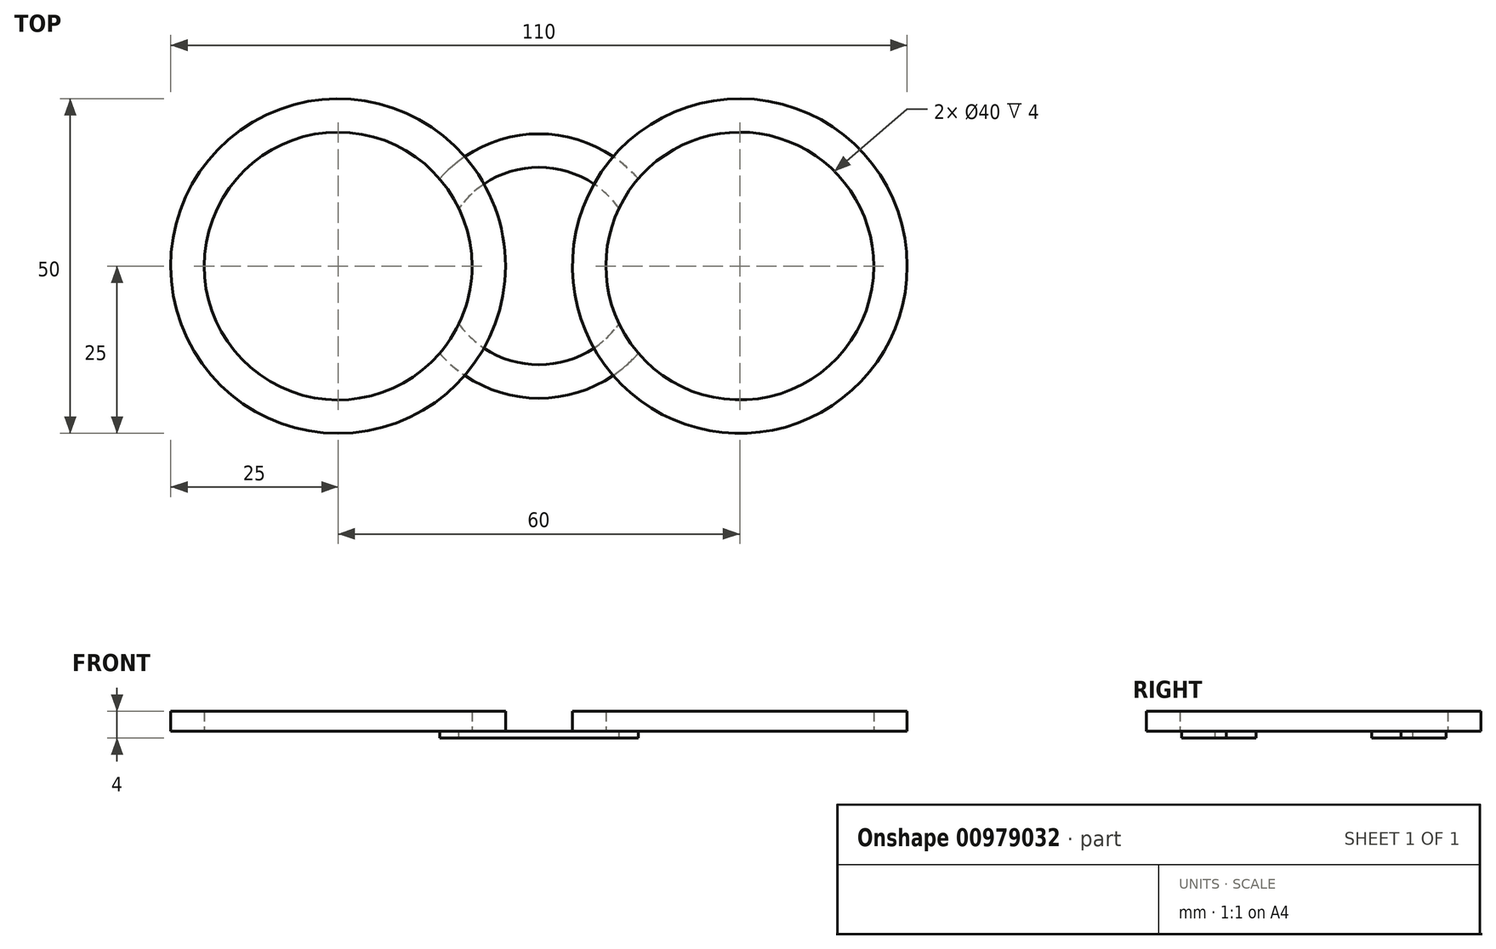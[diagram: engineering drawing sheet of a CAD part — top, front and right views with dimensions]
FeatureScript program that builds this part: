
annotation { "Feature Type Name" : "Feature", "Feature Type Description" : "" }
export const myFeature = defineFeature(function(context is Context, id is Id, definition is map)
    precondition{}
    {
        {
            var Q0;
            Q0=qCreatedBy(makeId("Top.planeOp"),FACE);
            var sketch = newSketch(context, id + "F0", { "sketchPlane" : qUnion([Q0])});
            skCircle(sketch, "E0", {"center": v(0, 0) * mm, "radius": 19.75 * mm});
            skCircle(sketch, "E1", {"center": v(0, 0) * mm, "radius": 14.75 * mm});
            skSolve(sketch);
        }
        {
            var Q0;
            Q0=makeQuery(id+"F0.imprint","IMPRINT",FACE,{"disambiguationData":[TD([[makeQuery(id+"F0.imprint","IMPRINT",EDGE,{"derivedFrom":sQuery(id+"F0.wireOp",EDGE,"E0")}),1.0]])]});
            extrude(context, id + "F1", {"entities" : qUnion([Q0]), "depth" : 1 * mm, "offsetDistance" : 25 * mm});
        }
        {
            var Q0;
            Q0=makeQuery(id+"F1.opExtrude","CAP_FACE",FACE,{"disambiguationData":[OSD([sQuery(id+"F0.wireOp",EDGE,"E0"),sQuery(id+"F0.wireOp",EDGE,"E1")])],"isStart":false});
            var sketch = newSketch(context, id + "F2", { "sketchPlane" : qUnion([Q0])});
            skCircle(sketch, "E2", {"center": v(-30, 0) * mm, "radius": 20 * mm});
            skCircle(sketch, "E3", {"center": v(30, 0) * mm, "radius": 20 * mm});
            skCircle(sketch, "E4", {"center": v(-30, 0) * mm, "radius": 25 * mm});
            skCircle(sketch, "E5", {"center": v(30, 0) * mm, "radius": 25 * mm});
            skSolve(sketch);
        }
        {
            var Q0;
            {var subQ0=sQuery(id+"F2.wireOp",EDGE,"E2");var subQ1=makeQuery(id+"F1.opExtrude","CAP_EDGE",EDGE,{"disambiguationData":[OSD([sQuery(id+"F0.wireOp",EDGE,"E0")])],"isStart":false});var subQ2=makeQuery(id+"F2.imprint","INTERSECT",VERTEX,{"disambiguationData":[OD(0.0)],"derivedFrom":[subQ1,subQ0]});Q0=makeQuery(id+"F2.imprint","IMPRINT",FACE,{"disambiguationData":[TD([[makeQuery(id+"F2.imprint","IMPRINT",EDGE,{"disambiguationData":[TD([[subQ2,-1.0]])],"derivedFrom":subQ0}),-1.0]])]});}
            var Q1;
            {var subQ0=sQuery(id+"F2.wireOp",EDGE,"E2");var subQ1=makeQuery(id+"F1.opExtrude","CAP_EDGE",EDGE,{"disambiguationData":[OSD([sQuery(id+"F0.wireOp",EDGE,"E1")])],"isStart":false});var subQ2=makeQuery(id+"F2.imprint","INTERSECT",VERTEX,{"disambiguationData":[OD(0.0)],"derivedFrom":[subQ1,subQ0]});Q1=makeQuery(id+"F2.imprint","IMPRINT",FACE,{"disambiguationData":[TD([[makeQuery(id+"F2.imprint","IMPRINT",EDGE,{"disambiguationData":[TD([[subQ2,1.0]])],"derivedFrom":subQ0}),-1.0]])]});}
            var Q2;
            {var subQ0=sQuery(id+"F2.wireOp",EDGE,"E2");var subQ1=makeQuery(id+"F1.opExtrude","CAP_EDGE",EDGE,{"disambiguationData":[OSD([sQuery(id+"F0.wireOp",EDGE,"E0")])],"isStart":false});var subQ2=makeQuery(id+"F2.imprint","INTERSECT",VERTEX,{"disambiguationData":[OD(0.0)],"derivedFrom":[subQ1,subQ0]});Q2=makeQuery(id+"F2.imprint","IMPRINT",FACE,{"disambiguationData":[TD([[makeQuery(id+"F2.imprint","IMPRINT",EDGE,{"disambiguationData":[TD([[subQ2,1.0]])],"derivedFrom":subQ0}),-1.0]])]});}
            var Q3;
            {var subQ0=sQuery(id+"F2.wireOp",EDGE,"E2");var subQ1=makeQuery(id+"F1.opExtrude","CAP_EDGE",EDGE,{"disambiguationData":[OSD([sQuery(id+"F0.wireOp",EDGE,"E0")])],"isStart":false});var subQ2=makeQuery(id+"F2.imprint","INTERSECT",VERTEX,{"disambiguationData":[OD(1.0)],"derivedFrom":[subQ1,subQ0]});Q3=makeQuery(id+"F2.imprint","IMPRINT",FACE,{"disambiguationData":[TD([[makeQuery(id+"F2.imprint","IMPRINT",EDGE,{"disambiguationData":[TD([[subQ2,-1.0]])],"derivedFrom":subQ0}),-1.0]])]});}
            var Q4;
            {var subQ0=sQuery(id+"F2.wireOp",EDGE,"E3");var subQ1=makeQuery(id+"F1.opExtrude","CAP_EDGE",EDGE,{"disambiguationData":[OSD([sQuery(id+"F0.wireOp",EDGE,"E0")])],"isStart":false});var subQ2=makeQuery(id+"F2.imprint","INTERSECT",VERTEX,{"disambiguationData":[OD(0.0)],"derivedFrom":[subQ1,subQ0]});Q4=makeQuery(id+"F2.imprint","IMPRINT",FACE,{"disambiguationData":[TD([[makeQuery(id+"F2.imprint","IMPRINT",EDGE,{"disambiguationData":[TD([[subQ2,1.0]])],"derivedFrom":subQ0}),-1.0]])]});}
            var Q5;
            {var subQ0=sQuery(id+"F2.wireOp",EDGE,"E3");var subQ1=makeQuery(id+"F1.opExtrude","CAP_EDGE",EDGE,{"disambiguationData":[OSD([sQuery(id+"F0.wireOp",EDGE,"E1")])],"isStart":false});var subQ2=makeQuery(id+"F2.imprint","INTERSECT",VERTEX,{"disambiguationData":[OD(1.0)],"derivedFrom":[subQ1,subQ0]});Q5=makeQuery(id+"F2.imprint","IMPRINT",FACE,{"disambiguationData":[TD([[makeQuery(id+"F2.imprint","IMPRINT",EDGE,{"disambiguationData":[TD([[subQ2,-1.0]])],"derivedFrom":subQ0}),-1.0]])]});}
            var Q6;
            {var subQ0=sQuery(id+"F2.wireOp",EDGE,"E3");var subQ1=makeQuery(id+"F1.opExtrude","CAP_EDGE",EDGE,{"disambiguationData":[OSD([sQuery(id+"F0.wireOp",EDGE,"E1")])],"isStart":false});var subQ2=makeQuery(id+"F2.imprint","INTERSECT",VERTEX,{"disambiguationData":[OD(0.0)],"derivedFrom":[subQ1,subQ0]});Q6=makeQuery(id+"F2.imprint","IMPRINT",FACE,{"disambiguationData":[TD([[makeQuery(id+"F2.imprint","IMPRINT",EDGE,{"disambiguationData":[TD([[subQ2,-1.0]])],"derivedFrom":subQ0}),-1.0]])]});}
            var Q7;
            {var subQ0=sQuery(id+"F2.wireOp",EDGE,"E3");var subQ1=makeQuery(id+"F1.opExtrude","CAP_EDGE",EDGE,{"disambiguationData":[OSD([sQuery(id+"F0.wireOp",EDGE,"E1")])],"isStart":false});var subQ2=makeQuery(id+"F2.imprint","INTERSECT",VERTEX,{"disambiguationData":[OD(0.0)],"derivedFrom":[subQ1,subQ0]});Q7=makeQuery(id+"F2.imprint","IMPRINT",FACE,{"disambiguationData":[TD([[makeQuery(id+"F2.imprint","IMPRINT",EDGE,{"disambiguationData":[TD([[subQ2,1.0]])],"derivedFrom":subQ0}),-1.0]])]});}
            extrude(context, id + "F3", {"entities" : qUnion([Q0, Q1, Q2, Q3, Q4, Q5, Q6, Q7]), "operationType" : NewBodyOperationType.ADD, "depth" : 3 * mm, "offsetDistance" : 25 * mm});
        }
        {
            var Q0;
            {var subQ0=sQuery(id+"F0.wireOp",EDGE,"E0");var subQ1=sQuery(id+"F0.wireOp",EDGE,"E1");var subQ2=sQuery(id+"F2.wireOp",EDGE,"E3");Q0=makeQuery(id+"F3.boolean.opBoolean","SPLIT",FACE,{"disambiguationData":[TD([makeQuery(id+"F1.opExtrude","SWEPT_FACE",FACE,{"disambiguationData":[OSD([subQ0])]}),makeQuery(id+"F1.opExtrude","SWEPT_FACE",FACE,{"disambiguationData":[OSD([subQ1])]}),makeQuery(id+"F3.opExtrude","SWEPT_FACE",FACE,{"disambiguationData":[OSD([subQ2])]}),makeQuery(id+"F3.opExtrude","CAP_FACE",FACE,{"disambiguationData":[OSD([subQ2,sQuery(id+"F2.wireOp",EDGE,"E5")])],"isStart":true})])],"derivedFrom":makeQuery(id+"F1.opExtrude","CAP_FACE",FACE,{"disambiguationData":[OSD([subQ0,subQ1])],"isStart":false})});}
            var Q1;
            {var subQ0=sQuery(id+"F0.wireOp",EDGE,"E0");var subQ1=sQuery(id+"F0.wireOp",EDGE,"E1");var subQ2=sQuery(id+"F2.wireOp",EDGE,"E2");Q1=makeQuery(id+"F3.boolean.opBoolean","SPLIT",FACE,{"disambiguationData":[TD([makeQuery(id+"F1.opExtrude","SWEPT_FACE",FACE,{"disambiguationData":[OSD([subQ0])]}),makeQuery(id+"F1.opExtrude","SWEPT_FACE",FACE,{"disambiguationData":[OSD([subQ1])]}),makeQuery(id+"F3.opExtrude","SWEPT_FACE",FACE,{"disambiguationData":[OSD([subQ2])]}),makeQuery(id+"F3.opExtrude","CAP_FACE",FACE,{"disambiguationData":[OSD([subQ2,sQuery(id+"F2.wireOp",EDGE,"E4")])],"isStart":true})])],"derivedFrom":makeQuery(id+"F1.opExtrude","CAP_FACE",FACE,{"disambiguationData":[OSD([subQ0,subQ1])],"isStart":false})});}
            extrude(context, id + "F4", {"entities" : qUnion([Q0, Q1]), "operationType" : NewBodyOperationType.REMOVE, "oppositeDirection" : true, "depth" : 25 * mm, "offsetDistance" : 25 * mm});
        }
    });
